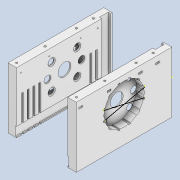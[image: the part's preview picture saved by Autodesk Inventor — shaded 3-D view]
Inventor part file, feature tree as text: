
AUTODESK INVENTOR PART (.ipt)
format: ipt  version: 2021 (Build 250183000, 183)  size: 1,248,768 bytes
history: native  units: mm
features: sketch x26, extrude x23, mirror x2, plane x1, chamfer x1
ambient origin geometry x8: Origin, YZ Plane, XZ Plane, XY Plane, X Axis, Y Axis, Z Axis, Center Point
bodies: Volumenkörper1 (feature_tree)
feature tree (53):
  extrude  "Extrusion1"  Depth=120.0mm
  extrude  "Extrusion2"  Depth=90.0mm
  extrude  "Extrusion3"  Depth=2.0mm
  extrude  "Extrusion4"  Depth=2.0mm
  extrude  "Extrusion5"  Depth=10.75mm
  extrude  "Extrusion6"  Depth=15.5mm
  extrude  "Extrusion7"  Depth=120.0mm
  extrude  "Extrusion8"  Depth=90.0mm TaperAngle=0.0deg
  extrude  "Extrusion9"  Depth=2.0mm
  extrude  "Extrusion10"  Depth=50.0mm
  extrude  "Extrusion11"  Depth=10.0mm TaperAngle=0.0deg
  extrude  "Extrusion12"  Depth=120.0mm
  sketch  "Skizze15"  dims[d43=2.7mm d44=2.7mm]
  sketch  "Skizze17"  dims[d45=2.7mm d46=105.0mm]
  sketch  "Skizze18"  dims[d47=30.0mm d48=0.0mm d57=60.0mm d59=119.175mm d60=60.0mm d62=10.0mm]
  sketch  "Skizze19"  dims[d65=64.0mm d66=0.0mm d67=116.0mm]
  extrude  "Extrusion13"  Depth=2.7mm
  extrude  "Extrusion14"  Depth=105.0mm
  extrude  "Extrusion15"  Depth=10.0mm
  plane  "Arbeitsebene1"
  extrude  "Extrusion16"  Depth=116.0mm
  extrude  "Extrusion17"  Depth=2.0mm
  extrude  "Extrusion18"  Depth=2.0mm TaperAngle=0.0deg
  extrude  "Extrusion19"  TaperAngle=45.0deg  [1 undecoded]
  mirror  "Mirror1"
  extrude  "Extrusion20"  TaperAngle=45.0deg  [1 undecoded]
  chamfer  "Chamfer1"  Distance=112.0mm
  extrude  "Extrusion21"  Depth=2.0mm TaperAngle=0.0deg
  mirror  "Mirror2"
  extrude  "Extrusion22"  Depth=15.0mm
  sketch  "Sketch30"  dims[d87=10.0mm d88=3.0mm d89=0.0mm]
  extrude  "Extrusion23"  Depth=3.0mm TaperAngle=0.0deg
  sketch  "Skizze1"  dims[d0=120.0mm d1=122.0mm]
  sketch  "Skizze2"  dims[d2=90.0mm d3=15.5mm]
  sketch  "Skizze3"  dims[d4=15.5mm d5=2.0mm]
  sketch  "Skizze4"  dims[d6=2.0mm d7=2.0mm]
  sketch  "Skizze5"  dims[d8=168.0mm d9=0.0mm d10=10.75mm]
  sketch  "Skizze7"  dims[d11=98.4mm d12=15.5mm]
  sketch  "Skizze9"  dims[d14=112.0mm d15=0.0mm d16=120.0mm]
  sketch  "Skizze10"  dims[d17=90.0mm d18=138.0mm d19=0.0mm]
  sketch  "Skizze11"  dims[d20=120.0mm d21=2.0mm]
  sketch  "Skizze12"  dims[d22=2.0mm d23=50.0mm d25=10.0mm d26=50.0mm d28=10.0mm]
  sketch  "Skizze13"  dims[d31=50.0mm d33=10.0mm d34=50.0mm d36=10.0mm d39=138.0mm d40=0.0mm]
  sketch  "Skizze14"  dims[d41=120.0mm d42=2.7mm]
  sketch  "Skizze20"  dims[d68=134.0mm d69=2.0mm]
  sketch  "Skizze21"  dims[d70=2.0mm d71=112.0mm d72=0.0mm]
  sketch  "Skizze24"  dims[d73=45.0deg d74=45.0deg]
  sketch  "Sketch25"  dims[d75=45.0deg d76=45.0deg]
  sketch  "Sketch26"  dims[d77=2.0mm]
  sketch  "Sketch27"  dims[d78=2.0mm d79=112.0mm d80=0.0mm]
  sketch  "Sketch28"  dims[d81=2.0mm d82=0.0mm d83=2.0mm d84=0.0mm]
  sketch  "Sketch29"  dims[d85=15.0mm d86=15.0mm]
  sketch  "Sketch31"  dims[d90=3.0mm d91=0.0mm d92=98.4mm d93=94.0mm d94=94.0mm d95=3.0mm d96=2.0mm d97=61.0mm d98=10.0mm d99=15.0mm d100=0.0mm d101=0.0mm d102=10.0mm d103=0.0mm d104=7.5mm d105=7.5mm d106=25.5mm d107=7.5mm d108=7.5mm d109=25.5mm d110=7.5mm d111=7.5mm d113=3.4mm d114=3.4mm d115=3.4mm d116=60.0mm d117=0.0mm d118=-10.0mm d119=5.7mm d120=5.7mm d123=2.6mm d124=0.0mm d126=60.0mm d128=60.0mm d129=3.4mm d130=135.0mm d131=50.0mm d132=50.0mm d133=3.4mm d134=3.4mm d135=7.5mm d136=7.5mm d137=25.5mm d138=7.5mm d139=7.5mm d140=25.5mm d141=7.5mm d142=7.5mm d143=3.4mm d144=3.4mm d145=3.4mm d146=3.4mm d147=135.0mm d156=5.7mm d157=5.7mm d158=3.4mm d159=3.4mm d161=1.6mm d162=1.6mm d163=0.0mm d164=0.0mm d165=3.4mm d166=3.4mm d167=3.4mm d168=3.4mm d169=3.4mm d170=3.4mm d171=3.4mm d172=3.4mm d173=7.5mm d174=7.5mm d175=25.5mm d176=7.5mm d177=7.5mm d178=25.5mm d179=7.5mm d180=7.5mm d181=3.4mm d182=3.4mm d183=3.4mm d184=3.4mm d185=135.0mm d186=50.0mm d187=50.0mm d188=3.4mm d189=3.4mm d190=3.4mm d191=3.4mm d192=3.4mm d193=3.4mm d194=3.4mm d195=3.4mm d196=5.7mm d197=5.7mm d198=3.4mm d199=3.4mm d200=3.4mm d201=3.4mm d202=5.7mm d203=5.7mm d204=3.4mm d205=3.4mm d206=1.6mm d207=1.6mm d208=70.05mm d209=22.5mm d210=0.0mm d211=0.0mm d212=70.05mm d213=22.5mm d214=13.0mm d215=0.0mm d217=40.0mm d218=10.0mm d219=360.0deg d220=0.0mm d221=0.0mm d222=1.5mm d223=2.0mm d224=45.0deg d226=120.0mm d227=3.0mm d228=74.0mm d229=360.0deg d235=13.0mm d236=0.0mm d238=120.0mm d245=120.0mm d246=120.0mm d248=360.0deg d251=12.0mm d252=30.0mm d253=30.0mm d254=0.0mm d255=0.0mm d257=60.0mm d259=60.0mm d261=60.0mm d263=60.0mm d265=60.0mm d267=60.0mm d269=60.0mm d271=60.0mm d272=0.0mm d273=0.0mm d54=0.5mm d55=0.872665mm d56=0.5mm]
note: 2 required parameter values undecoded (feature->parameter linkage not recoverable at this tier; creation-order binding heuristic only, values carry confidence <= 0.55)
